annotation { "Feature Type Name" : "Feature", "Feature Type Description" : "" }
export const myFeature = defineFeature(function(context is Context, id is Id, definition is map)
    precondition{}
    {
        {
            var Q0;
            Q0=qCreatedBy(makeId("Top.planeOp"),FACE);
            var sketch = newSketch(context, id + "F0", { "sketchPlane" : qUnion([Q0])});
            skLineSegment(sketch, "E0.bottom", {"start": v(-38.1, 50.8) * mm, "end": v(38.1, 50.8) * mm});
            skLineSegment(sketch, "E0.top", {"start": v(-38.1, -19.05) * mm, "end": v(38.1, -19.05) * mm});
            skLineSegment(sketch, "E0.left", {"start": v(-38.1, 50.8) * mm, "end": v(-38.1, -19.05) * mm});
            skLineSegment(sketch, "E0.right", {"start": v(38.1, 50.8) * mm, "end": v(38.1, -19.05) * mm});
            skSolve(sketch);
        }
        {
            var Q0;
            Q0 = qSketchRegion(id + "F0", true);
            extrude(context, id + "F1", {"entities" : qUnion([Q0]), "depth" : 3.17 * mm});
        }
        {
            var Q0;
            Q0=makeQuery(id+"F1.opExtrude","CAP_FACE",FACE,{"disambiguationData":[OSD([sQuery(id+"F0.wireOp",EDGE,"E0.bottom"),sQuery(id+"F0.wireOp",EDGE,"E0.top"),sQuery(id+"F0.wireOp",EDGE,"E0.left"),sQuery(id+"F0.wireOp",EDGE,"E0.right")])],"isStart":false});
            var sketch = newSketch(context, id + "F2", { "sketchPlane" : qUnion([Q0])});
            skLineSegment(sketch, "E1.bottom", {"start": v(-31.75, 44.45) * mm, "end": v(31.75, 44.45) * mm});
            skLineSegment(sketch, "E1.top", {"start": v(-31.75, 0) * mm, "end": v(31.75, 0) * mm});
            skLineSegment(sketch, "E1.left", {"start": v(-31.75, 44.45) * mm, "end": v(-31.75, 0) * mm});
            skLineSegment(sketch, "E1.right", {"start": v(31.75, 44.45) * mm, "end": v(31.75, 0) * mm});
            skLineSegment(sketch, "E2.0", {"start": v(-25.4, 38.1) * mm, "end": v(25.4, 38.1) * mm});
            skLineSegment(sketch, "E2.1", {"start": v(-25.4, 38.1) * mm, "end": v(-25.4, 6.35) * mm});
            skLineSegment(sketch, "E2.2", {"start": v(-25.4, 6.35) * mm, "end": v(25.4, 6.35) * mm});
            skLineSegment(sketch, "E2.3", {"start": v(25.4, 38.1) * mm, "end": v(25.4, 6.35) * mm});
            skSolve(sketch);
        }
        {
            var Q0;
            Q0 = qSketchRegion(id + "F2", true);
            extrude(context, id + "F3", {"entities" : qUnion([Q0]), "operationType" : NewBodyOperationType.ADD, "depth" : 38.1 * mm});
        }
        {
            var Q0;
            Q0=makeQuery(id+"F3.opExtrude","SWEPT_FACE",FACE,{"disambiguationData":[OSD([sQuery(id+"F2.wireOp",EDGE,"E1.top")])]});
            var sketch = newSketch(context, id + "F4", { "sketchPlane" : qUnion([Q0])});
            skLineSegment(sketch, "E3.bottom", {"start": v(-6.35, 22.23) * mm, "end": v(6.35, 22.23) * mm});
            skLineSegment(sketch, "E3.top", {"start": v(-6.35, 3.18) * mm, "end": v(6.35, 3.18) * mm});
            skLineSegment(sketch, "E3.left", {"start": v(-6.35, 22.23) * mm, "end": v(-6.35, 3.18) * mm});
            skLineSegment(sketch, "E3.right", {"start": v(6.35, 22.23) * mm, "end": v(6.35, 3.18) * mm});
            skLineSegment(sketch, "E4.bottom", {"start": v(-25.4, 25.4) * mm, "end": v(-12.7, 25.4) * mm});
            skLineSegment(sketch, "E4.top", {"start": v(-25.4, 9.53) * mm, "end": v(-12.7, 9.53) * mm});
            skLineSegment(sketch, "E4.left", {"start": v(-25.4, 25.4) * mm, "end": v(-25.4, 9.53) * mm});
            skLineSegment(sketch, "E4.right", {"start": v(-12.7, 25.4) * mm, "end": v(-12.7, 9.53) * mm});
            skLineSegment(sketch, "E5.MirrorCS", {"start": v(12.7, 25.4) * mm, "end": v(12.7, 9.53) * mm});
            skLineSegment(sketch, "E6.MirrorCS", {"start": v(25.4, 25.4) * mm, "end": v(25.4, 9.53) * mm});
            skLineSegment(sketch, "E7.MirrorCS", {"start": v(25.4, 9.53) * mm, "end": v(12.7, 9.53) * mm});
            skLineSegment(sketch, "E8.MirrorCS", {"start": v(25.4, 25.4) * mm, "end": v(12.7, 25.4) * mm});
            skSolve(sketch);
        }
        {
            var Q0;
            Q0 = qSketchRegion(id + "F4", true);
            extrude(context, id + "F5", {"entities" : qUnion([Q0]), "operationType" : NewBodyOperationType.REMOVE, "oppositeDirection" : true, "depth" : 3.17 * mm});
        }
        {
            var Q0;
            Q0=makeQuery(id+"F5.boolean.opBoolean","COPY",FACE,{"derivedFrom":makeQuery(id+"F5.opExtrude","CAP_FACE",FACE,{"disambiguationData":[OSD([sQuery(id+"F4.wireOp",EDGE,"E3.bottom"),sQuery(id+"F4.wireOp",EDGE,"E3.top"),sQuery(id+"F4.wireOp",EDGE,"E3.left"),sQuery(id+"F4.wireOp",EDGE,"E3.right")])],"isStart":false})});
            var sketch = newSketch(context, id + "F6", { "sketchPlane" : qUnion([Q0])});
            skLineSegment(sketch, "E9.bottom", {"start": v(-0.64, 22.23) * mm, "end": v(0.63, 22.23) * mm});
            skLineSegment(sketch, "E9.top", {"start": v(-0.64, 3.18) * mm, "end": v(0.63, 3.18) * mm});
            skLineSegment(sketch, "E9.left", {"start": v(-0.64, 22.23) * mm, "end": v(-0.64, 3.18) * mm});
            skLineSegment(sketch, "E9.right", {"start": v(0.63, 22.23) * mm, "end": v(0.63, 3.18) * mm});
            skLineSegment(sketch, "E10.bottom", {"start": v(-19.69, 25.4) * mm, "end": v(-18.42, 25.4) * mm});
            skLineSegment(sketch, "E10.top", {"start": v(-19.69, 9.53) * mm, "end": v(-18.42, 9.53) * mm});
            skLineSegment(sketch, "E10.left", {"start": v(-19.69, 25.4) * mm, "end": v(-19.69, 18.1) * mm});
            skLineSegment(sketch, "E10.right", {"start": v(-18.42, 25.4) * mm, "end": v(-18.42, 18.1) * mm});
            skLineSegment(sketch, "E11.bottom", {"start": v(-25.4, 18.1) * mm, "end": v(-19.69, 18.1) * mm});
            skLineSegment(sketch, "E11.top", {"start": v(-25.4, 16.83) * mm, "end": v(-19.69, 16.83) * mm});
            skLineSegment(sketch, "E11.left", {"start": v(-25.4, 18.1) * mm, "end": v(-25.4, 16.83) * mm});
            skLineSegment(sketch, "E11.right", {"start": v(-12.7, 18.1) * mm, "end": v(-12.7, 16.83) * mm});
            skLineSegment(sketch, "E12.trimOffspring", {"start": v(-18.42, 18.1) * mm, "end": v(-12.7, 18.1) * mm});
            skLineSegment(sketch, "E13.trimOffspring", {"start": v(-18.42, 16.83) * mm, "end": v(-18.42, 9.53) * mm});
            skLineSegment(sketch, "E14.trimOffspring", {"start": v(-18.42, 16.83) * mm, "end": v(-12.7, 16.83) * mm});
            skLineSegment(sketch, "E15.trimOffspring", {"start": v(-19.69, 16.83) * mm, "end": v(-19.69, 9.53) * mm});
            skLineSegment(sketch, "E16.MirrorCS", {"start": v(19.69, 25.4) * mm, "end": v(18.42, 25.4) * mm});
            skLineSegment(sketch, "E17.MirrorCS", {"start": v(19.69, 9.53) * mm, "end": v(18.42, 9.53) * mm});
            skLineSegment(sketch, "E18.MirrorCS", {"start": v(25.4, 18.1) * mm, "end": v(25.4, 16.83) * mm});
            skLineSegment(sketch, "E19.MirrorCS", {"start": v(12.7, 18.1) * mm, "end": v(12.7, 16.83) * mm});
            skLineSegment(sketch, "E20.MirrorCS", {"start": v(19.69, 25.4) * mm, "end": v(19.69, 18.1) * mm});
            skLineSegment(sketch, "E21.MirrorCS", {"start": v(18.42, 25.4) * mm, "end": v(18.42, 18.1) * mm});
            skLineSegment(sketch, "E22.MirrorCS", {"start": v(25.4, 18.1) * mm, "end": v(19.69, 18.1) * mm});
            skLineSegment(sketch, "E23.MirrorCS", {"start": v(25.4, 16.83) * mm, "end": v(19.69, 16.83) * mm});
            skLineSegment(sketch, "E24.MirrorCS", {"start": v(18.42, 18.1) * mm, "end": v(12.7, 18.1) * mm});
            skLineSegment(sketch, "E25.MirrorCS", {"start": v(18.42, 16.83) * mm, "end": v(18.42, 9.53) * mm});
            skLineSegment(sketch, "E26.MirrorCS", {"start": v(18.42, 16.83) * mm, "end": v(12.7, 16.83) * mm});
            skLineSegment(sketch, "E27.MirrorCS", {"start": v(19.69, 16.83) * mm, "end": v(19.69, 9.53) * mm});
            skCircle(sketch, "E28", {"center": v(1.9, 9.53) * mm, "radius": 0.64 * mm});
            skCircle(sketch, "E29.MirrorC", {"center": v(-1.9, 9.53) * mm, "radius": 0.64 * mm});
            skSolve(sketch);
        }
        {
            var Q0;
            Q0 = qSketchRegion(id + "F6", true);
            extrude(context, id + "F7", {"entities" : qUnion([Q0]), "operationType" : NewBodyOperationType.ADD, "depth" : 1.59 * mm});
        }
        {
            var Q0;
            Q0=makeQuery(id+"F3.opExtrude","SWEPT_FACE",FACE,{"disambiguationData":[OSD([sQuery(id+"F2.wireOp",EDGE,"E1.top")])]});
            var sketch = newSketch(context, id + "F8", { "sketchPlane" : qUnion([Q0])});
            skText(sketch, "E30", { "text": "TRAIN STATION", "fontName": "Arimo-Bold.ttf"});
            const initialGuessF8  = {"E30": [-0.0254, 0.03019, 1, 0, 0.00474]};
            skSetInitialGuess(sketch, initialGuessF8);
            skSolve(sketch);
        }
        {
            var Q0;
            Q0 = qSketchRegion(id + "F8", true);
            extrude(context, id + "F9", {"entities" : qUnion([Q0]), "operationType" : NewBodyOperationType.ADD, "depth" : 1.59 * mm});
        }
        {
            var Q0;
            {var subQ0=sQuery(id+"F0.wireOp",EDGE,"E0.left");var subQ1=sQuery(id+"F0.wireOp",EDGE,"E0.top");var subQ2=sQuery(id+"F0.wireOp",EDGE,"E0.right");var subQ3=sQuery(id+"F0.wireOp",EDGE,"E0.bottom");Q0=makeQuery(id+"F5.boolean.opBoolean","MERGE",FACE,{"derivedFrom":[makeQuery(id+"F3.boolean.opBoolean","SPLIT",FACE,{"disambiguationData":[TD([makeQuery(id+"F1.opExtrude","SWEPT_FACE",FACE,{"disambiguationData":[OSD([subQ3])]})])],"derivedFrom":makeQuery(id+"F1.opExtrude","CAP_FACE",FACE,{"disambiguationData":[OSD([subQ3,subQ1,subQ0,subQ2])],"isStart":false})}),makeQuery(id+"F5.opExtrude","SWEPT_FACE",FACE,{"disambiguationData":[OSD([sQuery(id+"F4.wireOp",EDGE,"E3.top")])]})]});}
            var sketch = newSketch(context, id + "F10", { "sketchPlane" : qUnion([Q0])});
            skLineSegment(sketch, "E31.bottom", {"start": v(-36.51, -5.08) * mm, "end": v(-34.93, -5.08) * mm});
            skLineSegment(sketch, "E31.top", {"start": v(-36.51, -19.05) * mm, "end": v(-34.93, -19.05) * mm});
            skLineSegment(sketch, "E31.left", {"start": v(-36.51, -5.08) * mm, "end": v(-36.51, -19.05) * mm});
            skLineSegment(sketch, "E31.right", {"start": v(-34.93, -5.08) * mm, "end": v(-34.93, -19.05) * mm});
            skLineSegment(sketch, "E32.1.0.0", {"start": v(-26.99, -5.08) * mm, "end": v(-26.99, -19.05) * mm});
            skLineSegment(sketch, "E32.1.0.1", {"start": v(-28.58, -5.08) * mm, "end": v(-28.58, -19.05) * mm});
            skLineSegment(sketch, "E32.1.0.2", {"start": v(-28.58, -5.08) * mm, "end": v(-26.99, -5.08) * mm});
            skLineSegment(sketch, "E32.1.0.3", {"start": v(-28.58, -19.05) * mm, "end": v(-26.99, -19.05) * mm});
            skLineSegment(sketch, "E32.2.0.0", {"start": v(-19.05, -5.08) * mm, "end": v(-19.05, -19.05) * mm});
            skLineSegment(sketch, "E32.2.0.1", {"start": v(-20.64, -5.08) * mm, "end": v(-20.64, -19.05) * mm});
            skLineSegment(sketch, "E32.2.0.2", {"start": v(-20.64, -5.08) * mm, "end": v(-19.05, -5.08) * mm});
            skLineSegment(sketch, "E32.2.0.3", {"start": v(-20.64, -19.05) * mm, "end": v(-19.05, -19.05) * mm});
            skLineSegment(sketch, "E32.3.0.0", {"start": v(-11.11, -5.08) * mm, "end": v(-11.11, -19.05) * mm});
            skLineSegment(sketch, "E32.3.0.1", {"start": v(-12.7, -5.08) * mm, "end": v(-12.7, -19.05) * mm});
            skLineSegment(sketch, "E32.3.0.2", {"start": v(-12.7, -5.08) * mm, "end": v(-11.11, -5.08) * mm});
            skLineSegment(sketch, "E32.3.0.3", {"start": v(-12.7, -19.05) * mm, "end": v(-11.11, -19.05) * mm});
            skLineSegment(sketch, "E32.4.0.0", {"start": v(-3.18, -5.08) * mm, "end": v(-3.18, -19.05) * mm});
            skLineSegment(sketch, "E32.4.0.1", {"start": v(-4.76, -5.08) * mm, "end": v(-4.76, -19.05) * mm});
            skLineSegment(sketch, "E32.4.0.2", {"start": v(-4.76, -5.08) * mm, "end": v(-3.18, -5.08) * mm});
            skLineSegment(sketch, "E32.4.0.3", {"start": v(-4.76, -19.05) * mm, "end": v(-3.18, -19.05) * mm});
            skLineSegment(sketch, "E32.5.0.0", {"start": v(4.76, -5.08) * mm, "end": v(4.76, -19.05) * mm});
            skLineSegment(sketch, "E32.5.0.1", {"start": v(3.17, -5.08) * mm, "end": v(3.17, -19.05) * mm});
            skLineSegment(sketch, "E32.5.0.2", {"start": v(3.17, -5.08) * mm, "end": v(4.76, -5.08) * mm});
            skLineSegment(sketch, "E32.5.0.3", {"start": v(3.17, -19.05) * mm, "end": v(4.76, -19.05) * mm});
            skLineSegment(sketch, "E32.6.0.0", {"start": v(12.7, -5.08) * mm, "end": v(12.7, -19.05) * mm});
            skLineSegment(sketch, "E32.6.0.1", {"start": v(11.11, -5.08) * mm, "end": v(11.11, -19.05) * mm});
            skLineSegment(sketch, "E32.6.0.2", {"start": v(11.11, -5.08) * mm, "end": v(12.7, -5.08) * mm});
            skLineSegment(sketch, "E32.6.0.3", {"start": v(11.11, -19.05) * mm, "end": v(12.7, -19.05) * mm});
            skLineSegment(sketch, "E32.7.0.0", {"start": v(20.64, -5.08) * mm, "end": v(20.64, -19.05) * mm});
            skLineSegment(sketch, "E32.7.0.1", {"start": v(19.05, -5.08) * mm, "end": v(19.05, -19.05) * mm});
            skLineSegment(sketch, "E32.7.0.2", {"start": v(19.05, -5.08) * mm, "end": v(20.64, -5.08) * mm});
            skLineSegment(sketch, "E32.7.0.3", {"start": v(19.05, -19.05) * mm, "end": v(20.64, -19.05) * mm});
            skLineSegment(sketch, "E32.8.0.0", {"start": v(28.57, -5.08) * mm, "end": v(28.57, -19.05) * mm});
            skLineSegment(sketch, "E32.8.0.1", {"start": v(26.99, -5.08) * mm, "end": v(26.99, -19.05) * mm});
            skLineSegment(sketch, "E32.8.0.2", {"start": v(26.99, -5.08) * mm, "end": v(28.57, -5.08) * mm});
            skLineSegment(sketch, "E32.8.0.3", {"start": v(26.99, -19.05) * mm, "end": v(28.57, -19.05) * mm});
            skLineSegment(sketch, "E32.9.0.0", {"start": v(36.51, -5.08) * mm, "end": v(36.51, -19.05) * mm});
            skLineSegment(sketch, "E32.9.0.1", {"start": v(34.93, -5.08) * mm, "end": v(34.93, -19.05) * mm});
            skLineSegment(sketch, "E32.9.0.2", {"start": v(34.92, -5.08) * mm, "end": v(36.51, -5.08) * mm});
            skLineSegment(sketch, "E32.9.0.3", {"start": v(34.92, -19.05) * mm, "end": v(36.51, -19.05) * mm});
            skLineSegment(sketch, "E32.direction1", {"start": v(-34.93, -19.05) * mm, "end": v(-28.58, -19.05) * mm, "construction": true});
            skSolve(sketch);
        }
        {
            var Q0;
            Q0 = qSketchRegion(id + "F10", true);
            extrude(context, id + "F11", {"entities" : qUnion([Q0]), "operationType" : NewBodyOperationType.ADD, "depth" : 0.95 * mm});
        }
        {
            var Q0;
            {var subQ0=sQuery(id+"F0.wireOp",EDGE,"E0.left");var subQ1=sQuery(id+"F0.wireOp",EDGE,"E0.top");var subQ2=sQuery(id+"F0.wireOp",EDGE,"E0.right");var subQ3=sQuery(id+"F0.wireOp",EDGE,"E0.bottom");Q0=makeQuery(id+"F5.boolean.opBoolean","MERGE",FACE,{"derivedFrom":[makeQuery(id+"F3.boolean.opBoolean","SPLIT",FACE,{"disambiguationData":[TD([makeQuery(id+"F1.opExtrude","SWEPT_FACE",FACE,{"disambiguationData":[OSD([subQ3])]})])],"derivedFrom":makeQuery(id+"F1.opExtrude","CAP_FACE",FACE,{"disambiguationData":[OSD([subQ3,subQ1,subQ0,subQ2])],"isStart":false})}),makeQuery(id+"F5.opExtrude","SWEPT_FACE",FACE,{"disambiguationData":[OSD([sQuery(id+"F4.wireOp",EDGE,"E3.top")])]})]});}
            var sketch = newSketch(context, id + "F12", { "sketchPlane" : qUnion([Q0])});
            skLineSegment(sketch, "E33.bottom", {"start": v(-38.1, -5.71) * mm, "end": v(38.1, -5.71) * mm});
            skLineSegment(sketch, "E33.top", {"start": v(-38.1, -8.89) * mm, "end": v(38.1, -8.89) * mm});
            skLineSegment(sketch, "E33.left", {"start": v(-38.1, -5.71) * mm, "end": v(-38.1, -8.89) * mm});
            skLineSegment(sketch, "E33.right", {"start": v(38.1, -5.71) * mm, "end": v(38.1, -8.89) * mm});
            skLineSegment(sketch, "E34.bottom", {"start": v(-38.1, -18.41) * mm, "end": v(38.1, -18.41) * mm});
            skLineSegment(sketch, "E34.top", {"start": v(-38.1, -15.24) * mm, "end": v(38.1, -15.24) * mm});
            skLineSegment(sketch, "E34.left", {"start": v(-38.1, -18.41) * mm, "end": v(-38.1, -15.24) * mm});
            skLineSegment(sketch, "E34.right", {"start": v(38.1, -18.41) * mm, "end": v(38.1, -15.24) * mm});
            skLineSegment(sketch, "E35", {"start": v(36.51, -12.06) * mm, "end": v(-36.51, -12.06) * mm, "construction": true});
            skSolve(sketch);
        }
        {
            var Q0;
            Q0 = qSketchRegion(id + "F12", true);
            extrude(context, id + "F13", {"entities" : qUnion([Q0]), "operationType" : NewBodyOperationType.ADD, "depth" : 1.59 * mm});
        }
        {
            var Q0;
            Q0=makeQuery(id+"F3.opExtrude","CAP_EDGE",EDGE,{"disambiguationData":[OSD([sQuery(id+"F2.wireOp",EDGE,"E1.right")])],"isStart":false});
            var Q1;
            Q1=makeQuery(id+"F3.opExtrude","CAP_EDGE",EDGE,{"disambiguationData":[OSD([sQuery(id+"F2.wireOp",EDGE,"E1.bottom")])],"isStart":false});
            var Q2;
            Q2=makeQuery(id+"F3.opExtrude","CAP_EDGE",EDGE,{"disambiguationData":[OSD([sQuery(id+"F2.wireOp",EDGE,"E1.left")])],"isStart":false});
            var Q3;
            Q3=makeQuery(id+"F3.opExtrude","CAP_EDGE",EDGE,{"disambiguationData":[OSD([sQuery(id+"F2.wireOp",EDGE,"E1.top")])],"isStart":false});
            chamfer(context, id + "F14", {"entities" : qUnion([Q0, Q1, Q2, Q3]), "width" : 1.59 * mm, "tangentPropagation" : true});
        }
        {
            var Q0;
            Q0=makeQuery(id+"F3.opExtrude","SWEPT_FACE",FACE,{"disambiguationData":[OSD([sQuery(id+"F2.wireOp",EDGE,"E2.1")])]});
            var sketch = newSketch(context, id + "F15", { "sketchPlane" : qUnion([Q0])});
            skCircle(sketch, "E36", {"center": v(6.35, 37.52) * mm, "radius": 1.27 * mm});
            skCircle(sketch, "E37", {"center": v(38.1, 37.52) * mm, "radius": 1.27 * mm});
            skLineSegment(sketch, "E38", {"start": v(6.35, 37.52) * mm, "end": v(38.1, 37.52) * mm, "construction": true});
            skLineSegment(sketch, "E39", {"start": v(22.22, 41.27) * mm, "end": v(22.22, 37.52) * mm, "construction": true});
            skSolve(sketch);
        }
        {
            var Q0;
            Q0 = qSketchRegion(id + "F15", true);
            var Q1;
            Q1=makeQuery(id+"F3.opExtrude","SWEPT_FACE",FACE,{"disambiguationData":[OSD([sQuery(id+"F2.wireOp",EDGE,"E2.3")])]});
            extrude(context, id + "F16", {"entities" : qUnion([Q0]), "operationType" : NewBodyOperationType.REMOVE, "endBound" : BoundingType.UP_TO_SURFACE, "endBoundEntityFace" : qUnion([Q1]), "depth" : 25.4 * mm});
        }
        {
            var Q0;
            Q0=makeQuery(id+"F16.boolean.opBoolean","INTERSECT",EDGE,{"disambiguationData":[OD(0.0)],"derivedFrom":[makeQuery(id+"F3.opExtrude","SWEPT_FACE",FACE,{"disambiguationData":[OSD([sQuery(id+"F2.wireOp",EDGE,"E2.2")])]}),makeQuery(id+"F16.opExtrude","SWEPT_FACE",FACE,{"disambiguationData":[OSD([sQuery(id+"F15.wireOp",EDGE,"E36")])]})]});
            var Q1;
            Q1=makeQuery(id+"F16.boolean.opBoolean","INTERSECT",EDGE,{"disambiguationData":[OD(0.0)],"derivedFrom":[makeQuery(id+"F3.opExtrude","SWEPT_FACE",FACE,{"disambiguationData":[OSD([sQuery(id+"F2.wireOp",EDGE,"E2.0")])]}),makeQuery(id+"F16.opExtrude","SWEPT_FACE",FACE,{"disambiguationData":[OSD([sQuery(id+"F15.wireOp",EDGE,"E37")])]})]});
            chamfer(context, id + "F17", {"entities" : qUnion([Q0, Q1]), "width" : 0.83 * mm, "tangentPropagation" : true});
        }
        {
            var Q0;
            Q0=makeQuery(id+"F3.opExtrude","CAP_EDGE",EDGE,{"disambiguationData":[OSD([sQuery(id+"F2.wireOp",EDGE,"E2.1")])],"isStart":false});
            var Q1;
            Q1=makeQuery(id+"F3.opExtrude","CAP_EDGE",EDGE,{"disambiguationData":[OSD([sQuery(id+"F2.wireOp",EDGE,"E2.2")])],"isStart":false});
            var Q2;
            Q2=makeQuery(id+"F3.opExtrude","CAP_EDGE",EDGE,{"disambiguationData":[OSD([sQuery(id+"F2.wireOp",EDGE,"E2.3")])],"isStart":false});
            var Q3;
            Q3=makeQuery(id+"F3.opExtrude","CAP_EDGE",EDGE,{"disambiguationData":[OSD([sQuery(id+"F2.wireOp",EDGE,"E2.0")])],"isStart":false});
            chamfer(context, id + "F18", {"entities" : qUnion([Q0, Q1, Q2, Q3]), "width" : 0.76 * mm, "tangentPropagation" : true});
        }
    });